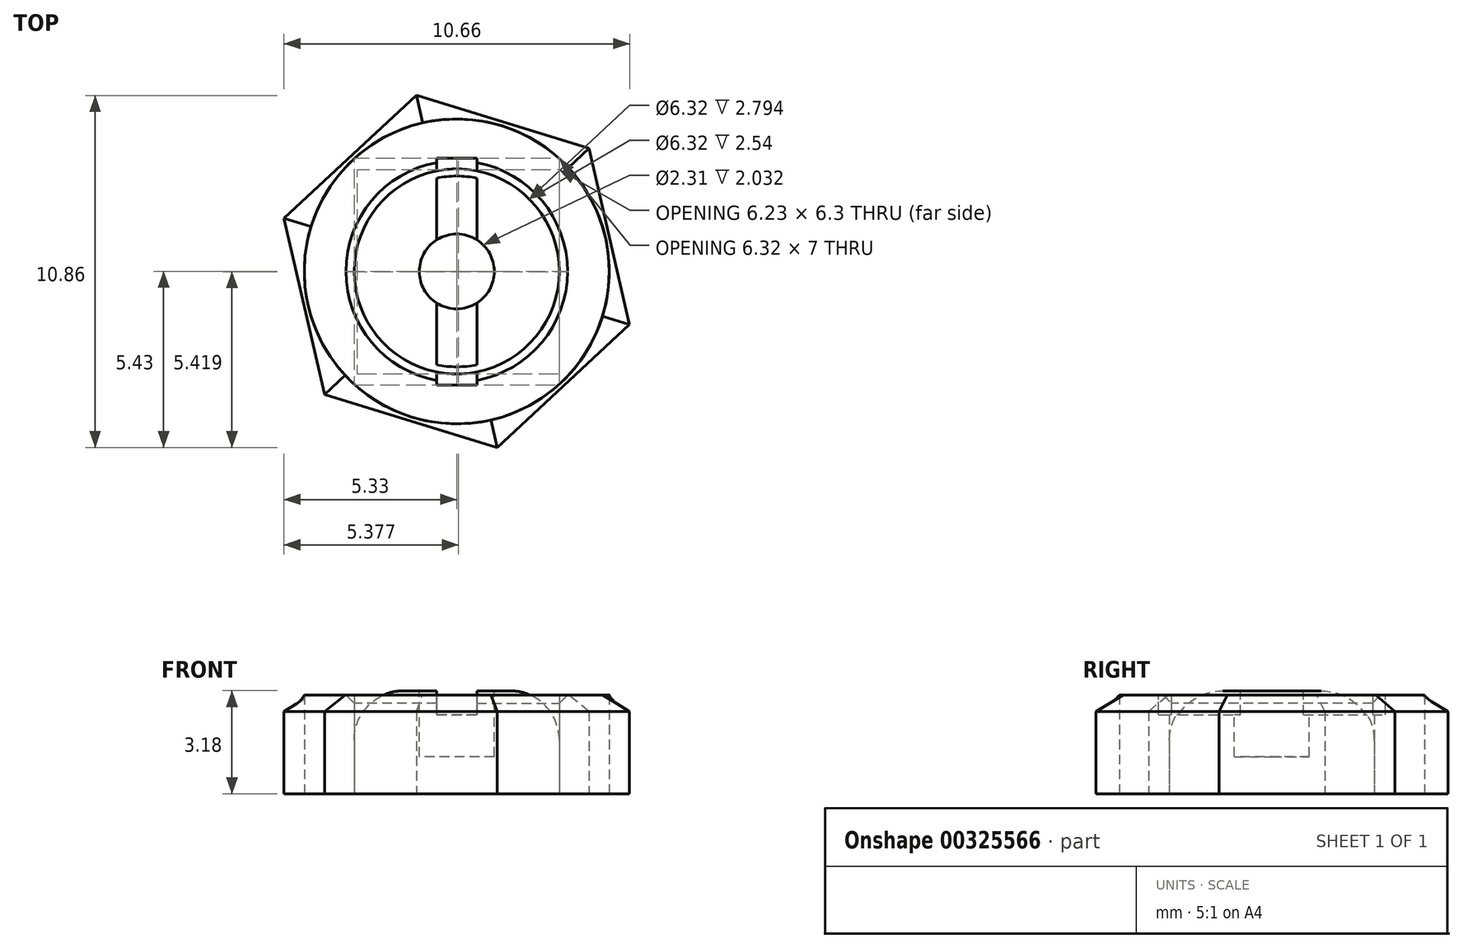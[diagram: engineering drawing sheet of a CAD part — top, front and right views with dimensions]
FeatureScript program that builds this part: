
annotation { "Feature Type Name" : "Feature", "Feature Type Description" : "" }
export const myFeature = defineFeature(function(context is Context, id is Id, definition is map)
    precondition{}
    {
        {
            var Q0;
            Q0=qCreatedBy(makeId("Top.planeOp"),FACE);
            var sketch = newSketch(context, id + "F0", { "sketchPlane" : qUnion([Q0])});
            skCircle(sketch, "E0.cCircle", {"center": v(0, 0) * mm, "radius": 4.83 * mm, "construction": true});
            skLineSegment(sketch, "E0.0", {"start": v(5.33, -1.63) * mm, "end": v(1.25, -5.43) * mm});
            skLineSegment(sketch, "E0.1", {"start": v(1.25, -5.43) * mm, "end": v(-4.08, -3.8) * mm});
            skLineSegment(sketch, "E0.2", {"start": v(-4.08, -3.8) * mm, "end": v(-5.33, 1.63) * mm});
            skLineSegment(sketch, "E0.3", {"start": v(-5.33, 1.63) * mm, "end": v(-1.25, 5.43) * mm});
            skLineSegment(sketch, "E0.4", {"start": v(-1.25, 5.43) * mm, "end": v(4.08, 3.8) * mm});
            skLineSegment(sketch, "E0.5", {"start": v(4.08, 3.8) * mm, "end": v(5.33, -1.63) * mm});
            skPoint(sketch, "E0.0.midPoint", {"position": v(3.29, -3.53) * mm});
            skSolve(sketch);
        }
        {
            var Q0;
            Q0=qCreatedBy(makeId("Top.planeOp"),FACE);
            var sketch = newSketch(context, id + "F1", { "sketchPlane" : qUnion([Q0])});
            skCircle(sketch, "E1", {"center": v(0, 0) * mm, "radius": 4.7 * mm});
            skSolve(sketch);
        }
        {
            var Q0;
            Q0=qCreatedBy(makeId("Top.planeOp"),FACE);
            var sketch = newSketch(context, id + "F2", { "sketchPlane" : qUnion([Q0])});
            skCircle(sketch, "E2", {"center": v(0, 0) * mm, "radius": 3.16 * mm});
            skSolve(sketch);
        }
        {
            var Q0;
            Q0=makeQuery(id+"F0.imprint","IMPRINT",FACE,{"disambiguationData":[TD([[makeQuery(id+"F0.imprint","IMPRINT",EDGE,{"derivedFrom":sQuery(id+"F0.wireOp",EDGE,"E0.0")}),-1.0]])]});
            extrude(context, id + "F3", {"entities" : qUnion([Q0]), "depth" : 2.54 * mm});
        }
        {
            var Q0;
            Q0=qSketchRegion(id+"F1",true);
            extrude(context, id + "F4", {"entities" : qUnion([Q0]), "depth" : 3.05 * mm});
        }
        {
            var Q0;
            Q0=makeQuery(id+"F3.opExtrude","CAP_FACE",FACE,{"disambiguationData":[OSD([sQuery(id+"F0.wireOp",EDGE,"E0.0"),sQuery(id+"F0.wireOp",EDGE,"E0.1"),sQuery(id+"F0.wireOp",EDGE,"E0.2"),sQuery(id+"F0.wireOp",EDGE,"E0.3"),sQuery(id+"F0.wireOp",EDGE,"E0.4"),sQuery(id+"F0.wireOp",EDGE,"E0.5")])],"isStart":false});
            var Q1;
            Q1=makeQuery(id+"F4.opExtrude","CAP_FACE",FACE,{"disambiguationData":[OSD([sQuery(id+"F1.wireOp",EDGE,"E1")])],"isStart":false});
            loft(context, id + "F5", {"sheetProfilesArray" : [{ "sheetProfileEntities" : qUnion([Q0]) }, { "sheetProfileEntities" : qUnion([Q1]) }]});
        }
        {
            var Q0;
            Q0=qSketchRegion(id+"F2",true);
            extrude(context, id + "F6", {"entities" : qUnion([Q0]), "operationType" : NewBodyOperationType.REMOVE, "depth" : 5.08 * mm});
        }
        {
            var Q0;
            Q0=makeQuery(id+"F6.boolean.opBoolean","INTERSECT",EDGE,{"derivedFrom":[makeQuery(id+"F4.opExtrude","CAP_FACE",FACE,{"disambiguationData":[OSD([sQuery(id+"F1.wireOp",EDGE,"E1")])],"isStart":false}),makeQuery(id+"F6.opExtrude","SWEPT_FACE",FACE,{"disambiguationData":[OSD([sQuery(id+"F2.wireOp",EDGE,"E2")])]})]});
            chamfer(context, id + "F7", {"entities" : qUnion([Q0]), "width" : 0.25 * mm, "tangentPropagation" : true});
        }
        {
            var Q0;
            Q0=qSketchRegion(id+"F2",true);
            extrude(context, id + "F8", {"entities" : qUnion([Q0]), "depth" : 3.17 * mm});
        }
        {
            var Q0;
            Q0=makeQuery(id+"F8.opExtrude","CAP_EDGE",EDGE,{"disambiguationData":[OSD([sQuery(id+"F2.wireOp",EDGE,"E2")])],"isStart":false});
            fillet(context, id + "F9", {"entities" : qUnion([Q0]), "radius" : 1.52 * mm, "tangentPropagation" : true, "allowEdgeOverflow" : false});
        }
        {
            var Q0;
            Q0=makeQuery(id+"F8.opExtrude","CAP_FACE",FACE,{"disambiguationData":[OSD([sQuery(id+"F2.wireOp",EDGE,"E2")])],"isStart":false});
            var sketch = newSketch(context, id + "F10", { "sketchPlane" : qUnion([Q0])});
            skLineSegment(sketch, "E3.bottom", {"start": v(0.62, -3.5) * mm, "end": v(-0.62, -3.5) * mm});
            skLineSegment(sketch, "E3.top", {"start": v(0.62, 3.5) * mm, "end": v(-0.62, 3.5) * mm});
            skLineSegment(sketch, "E3.left", {"start": v(0.62, -3.5) * mm, "end": v(0.62, 3.5) * mm});
            skLineSegment(sketch, "E3.right", {"start": v(-0.62, -3.5) * mm, "end": v(-0.62, 3.5) * mm});
            skPoint(sketch, "E3.middle", {"position": v(0, 0) * mm});
            skSolve(sketch);
        }
        {
            var Q0;
            Q0=qSketchRegion(id+"F10",true);
            extrude(context, id + "F11", {"entities" : qUnion([Q0]), "operationType" : NewBodyOperationType.REMOVE, "oppositeDirection" : true, "depth" : 0.74 * mm});
        }
        {
            var Q0;
            {var subQ0=sQuery(id+"F2.wireOp",EDGE,"E2");Q0=makeQuery(id+"F11.boolean.opBoolean","SPLIT",FACE,{"disambiguationData":[TD([makeQuery(id+"F11.opExtrude","SWEPT_FACE",FACE,{"disambiguationData":[OSD([sQuery(id+"F10.wireOp",EDGE,"E3.left")])]})])],"derivedFrom":makeQuery(id+"F8.opExtrude","CAP_FACE",FACE,{"disambiguationData":[OSD([subQ0])],"isStart":false})});}
            var sketch = newSketch(context, id + "F12", { "sketchPlane" : qUnion([Q0])});
            skCircle(sketch, "E4", {"center": v(0, 0) * mm, "radius": 1.16 * mm});
            skSolve(sketch);
        }
        {
            var Q0;
            Q0=qSketchRegion(id+"F12",true);
            extrude(context, id + "F13", {"entities" : qUnion([Q0]), "operationType" : NewBodyOperationType.REMOVE, "oppositeDirection" : true, "depth" : 2.03 * mm});
        }
    });
